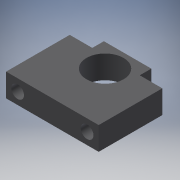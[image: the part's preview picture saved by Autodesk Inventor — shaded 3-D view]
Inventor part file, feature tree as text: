
AUTODESK INVENTOR PART (.ipt)
format: ipt  version: 2018 (Build 220112000, 112)  size: 153,088 bytes
history: native  units: mm
features: other x14, sketch x4, extrude x2, hole x2
ambient origin geometry x8: Origin, YZ Plane, XZ Plane, XY Plane, X Axis, Y Axis, Z Axis, Center Point
bodies: Solid1 (feature_tree)
feature tree (22):
  extrude  "Extrusion1"  TaperAngle=0.0deg  [1 undecoded]
  hole  "Hole3"  [1 undecoded]
  other  "bf_1_XY"
  other  "bf_1_YZ"
  other  "bf_1_ZX"
  other  "bf_1_X"
  other  "bf_1_Y"
  other  "bf_1_Z"
  other  "bf_1_Center"
  other  "bf_2x_XY"
  other  "bf_2x_YZ"
  other  "bf_2x_ZX"
  other  "bf_2x_X"
  other  "bf_2x_Y"
  other  "bf_2x_Z"
  other  "bf_2x_Center"
  hole  "Hole4"  [1 undecoded]
  extrude  "Extrusion2"  Depth=19.5mm
  sketch  "Sketch_1"  dims[d0=20.0mm d1=0.0mm]
  sketch  "Sketch4"  dims[d16=32.0mm d17=6.0mm d18=4.0mm d19=2.0mm d20=90.0deg d21=20.0mm d22=0.0mm d23=0.0mm]
  sketch  "Sketch6"  dims[d29=19.5mm]
  sketch  "Sketch9"  dims[d35=11.0mm d36=6.0mm d37=17.0mm d38=12.0mm d39=90.0deg d40=8.0mm d41=20.594885mm d42=10.0mm d43=41.0mm d44=19.5mm d45=10.0mm d46=10.0mm d47=10.0mm d48=11.0mm d49=11.0mm d50=25.0mm d51=0.0mm d54=30.0mm d55=0.0mm]
note: 3 required parameter values undecoded (feature->parameter linkage not recoverable at this tier; creation-order binding heuristic only, values carry confidence <= 0.55)
